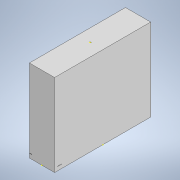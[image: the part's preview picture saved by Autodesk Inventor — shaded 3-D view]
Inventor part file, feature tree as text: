
AUTODESK INVENTOR PART (.ipt)
format: ipt  version: 2021 (Build 250183000, 183)  size: 117,248 bytes
history: native  units: mm
features: sketch x7, extrude x1
ambient origin geometry x8: Origin, YZ Plane, XZ Plane, XY Plane, X Axis, Y Axis, Z Axis, Center Point
bodies: Solid1 (feature_tree)
feature tree (8):
  extrude  "Extrusion1"  Depth=1067.0mm
  sketch  "Sketch2"  dims[d2=533.5mm]
  sketch  "Sketch3"  dims[d3=140.0mm]
  sketch  "Sketch4"  dims[d4=914.0mm]
  sketch  "Sketch5"  dims[d5=0.0mm]
  sketch  "Sketch6"
  sketch  "Sketch7"
  sketch  "Sketch1"  dims[d0=280.0mm d1=1067.0mm]
